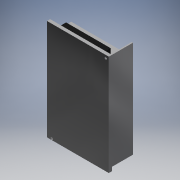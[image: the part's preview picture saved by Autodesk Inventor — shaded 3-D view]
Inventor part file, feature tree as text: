
AUTODESK INVENTOR PART (.ipt)
format: ipt  version: 2018 (Build 220112000, 112)  size: 145,408 bytes
history: native  units: mm
features: extrude x5, sketch x5
ambient origin geometry x8: Origin, YZ Plane, XZ Plane, XY Plane, X Axis, Y Axis, Z Axis, Center Point
bodies: Solid1 (feature_tree)
feature tree (10):
  extrude  "Extrusion1"  Depth=158.0mm
  extrude  "Extrusion2"  Depth=5.0mm
  extrude  "Extrusion3"  Depth=89.5mm
  extrude  "Extrusion4"  Depth=4.5mm
  extrude  "Extrusion5"  Depth=5.0mm TaperAngle=0.0deg
  sketch  "Sketch1"  dims[d0=97.0mm d1=158.0mm]
  sketch  "Sketch2"  dims[d2=5.0mm d3=0.0mm d4=3.5mm]
  sketch  "Sketch3"  dims[d5=155.75mm d6=89.5mm]
  sketch  "Sketch4"  dims[d7=3.5mm d8=4.5mm]
  sketch  "Sketch5"  dims[d9=5.0mm d10=5.0mm d11=0.0mm d12=6.0mm d13=20.0mm d14=33.0mm d15=0.0mm d16=2.0mm d17=20.0mm d18=0.0mm d19=70.0mm d20=10.0mm d21=7.0mm d22=15.0mm d23=0.0mm]
